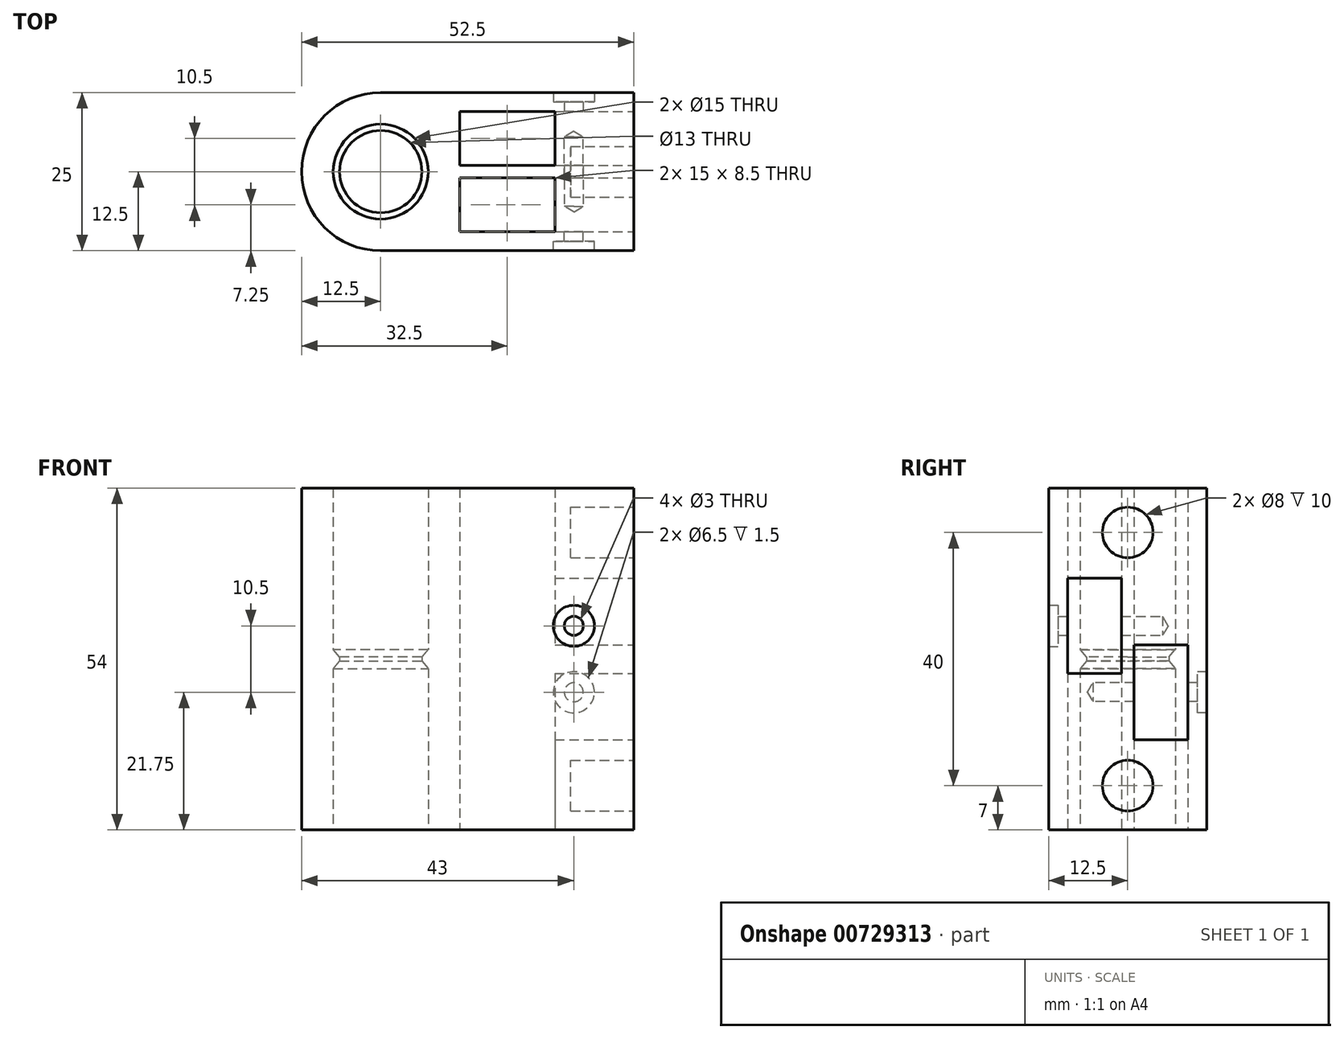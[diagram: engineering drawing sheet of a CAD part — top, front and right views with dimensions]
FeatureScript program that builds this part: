
annotation { "Feature Type Name" : "Feature", "Feature Type Description" : "" }
export const myFeature = defineFeature(function(context is Context, id is Id, definition is map)
    precondition{}
    {
        {
            var Q0;
            Q0=qCreatedBy(makeId("Top.planeOp"),FACE);
            var sketch = newSketch(context, id + "F0", { "sketchPlane" : qUnion([Q0])});
            skLineSegment(sketch, "E0.bottom", {"start": v(0, 0) * mm, "end": v(40, 0) * mm});
            skLineSegment(sketch, "E0.top", {"start": v(0, 25) * mm, "end": v(40, 25) * mm});
            skLineSegment(sketch, "E0.left", {"start": v(0, 0) * mm, "end": v(0, 25) * mm});
            skLineSegment(sketch, "E0.right", {"start": v(40, 0) * mm, "end": v(40, 25) * mm});
            skArc(sketch, "E1", {"start": v(0, 25) * mm, "mid": v(-12.5, 12.5) * mm, "end": v(0, 0) * mm});
            skCircle(sketch, "E2", {"center": v(0, 12.5) * mm, "radius": 7.5 * mm});
            skLineSegment(sketch, "E3.bottom", {"start": v(12.5, 22) * mm, "end": v(27.5, 22) * mm});
            skLineSegment(sketch, "E3.top", {"start": v(12.5, 3) * mm, "end": v(27.5, 3) * mm});
            skLineSegment(sketch, "E3.left", {"start": v(12.5, 22) * mm, "end": v(12.5, 3) * mm});
            skLineSegment(sketch, "E3.right", {"start": v(27.5, 22) * mm, "end": v(27.5, 3) * mm});
            skPoint(sketch, "E4", {"position": v(7.5, 12.5) * mm});
            skLineSegment(sketch, "E5.bottom", {"start": v(12.5, 13.5) * mm, "end": v(27.5, 13.5) * mm});
            skLineSegment(sketch, "E5.top", {"start": v(12.5, 11.5) * mm, "end": v(27.5, 11.5) * mm});
            skLineSegment(sketch, "E5.left", {"start": v(12.5, 13.5) * mm, "end": v(12.5, 11.5) * mm});
            skLineSegment(sketch, "E5.right", {"start": v(27.5, 13.5) * mm, "end": v(27.5, 11.5) * mm});
            skPoint(sketch, "E6", {"position": v(12.5, 12.5) * mm});
            skSolve(sketch);
        }
        {
            var Q0;
            {var subQ5=sQuery(id+"F0.wireOp",EDGE,"E0.bottom");Q0=makeQuery(id+"F0.imprint","IMPRINT",FACE,{"disambiguationData":[TD([[makeQuery(id+"F0.imprint","IMPRINT",EDGE,{"derivedFrom":subQ5}),1.0]])]});}
            var Q1;
            {var subQ0=sQuery(id+"F0.wireOp",EDGE,"E1");Q1=makeQuery(id+"F0.imprint","IMPRINT",FACE,{"disambiguationData":[TD([[makeQuery(id+"F0.imprint","IMPRINT",EDGE,{"derivedFrom":subQ0}),1.0]])]});}
            var Q2;
            {var subQ2=sQuery(id+"F0.wireOp",EDGE,"E5.bottom");Q2=makeQuery(id+"F0.imprint","IMPRINT",FACE,{"disambiguationData":[TD([[makeQuery(id+"F0.imprint","IMPRINT",EDGE,{"derivedFrom":subQ2}),-1.0]])]});}
            extrude(context, id + "F1", {"entities" : qUnion([Q0, Q1, Q2]), "depth" : 54 * mm, "offsetDistance" : 25 * mm});
        }
        {
            var Q0;
            Q0=makeQuery(id+"F1.opExtrude","SWEPT_FACE",FACE,{"disambiguationData":[OSD([sQuery(id+"F0.wireOp",EDGE,"E0.right")])]});
            var sketch = newSketch(context, id + "F2", { "sketchPlane" : qUnion([Q0])});
            skLineSegment(sketch, "E7.bottom", {"start": v(3, 39.75) * mm, "end": v(11.5, 39.75) * mm});
            skLineSegment(sketch, "E7.top", {"start": v(3, 24.75) * mm, "end": v(11.5, 24.75) * mm});
            skLineSegment(sketch, "E7.left", {"start": v(3, 39.75) * mm, "end": v(3, 24.75) * mm});
            skLineSegment(sketch, "E7.right", {"start": v(11.5, 39.75) * mm, "end": v(11.5, 24.75) * mm});
            skLineSegment(sketch, "E8.bottom", {"start": v(13.5, 29.25) * mm, "end": v(22, 29.25) * mm});
            skLineSegment(sketch, "E8.top", {"start": v(13.5, 14.25) * mm, "end": v(22, 14.25) * mm});
            skLineSegment(sketch, "E8.left", {"start": v(13.5, 29.25) * mm, "end": v(13.5, 14.25) * mm});
            skLineSegment(sketch, "E8.right", {"start": v(22, 29.25) * mm, "end": v(22, 14.25) * mm});
            skPoint(sketch, "E9", {"position": v(13.5, 27) * mm});
            skPoint(sketch, "E10", {"position": v(25, 27) * mm});
            skSolve(sketch);
        }
        {
            var Q0;
            Q0=makeQuery(id+"F2.imprint","IMPRINT",FACE,{"disambiguationData":[TD([[makeQuery(id+"F2.imprint","IMPRINT",EDGE,{"derivedFrom":sQuery(id+"F2.wireOp",EDGE,"E7.bottom")}),-1.0]])]});
            var Q1;
            Q1=makeQuery(id+"F2.imprint","IMPRINT",FACE,{"disambiguationData":[TD([[makeQuery(id+"F2.imprint","IMPRINT",EDGE,{"derivedFrom":sQuery(id+"F2.wireOp",EDGE,"E8.bottom")}),-1.0]])]});
            extrude(context, id + "F3", {"entities" : qUnion([Q0, Q1]), "operationType" : NewBodyOperationType.REMOVE, "endBound" : BoundingType.UP_TO_NEXT, "oppositeDirection" : true, "depth" : 25 * mm, "offsetDistance" : 25 * mm});
        }
        {
            var Q0;
            Q0=makeQuery(id+"F1.opExtrude","SWEPT_FACE",FACE,{"disambiguationData":[OSD([sQuery(id+"F0.wireOp",EDGE,"E0.bottom")])]});
            var sketch = newSketch(context, id + "F4", { "sketchPlane" : qUnion([Q0])});
            skPoint(sketch, "E11", {"position": v(30.5, 32.25) * mm});
            skSolve(sketch);
        }
        {
            var Q0;
            Q0=sQuery(id+"F4.wireOp",VERTEX,"E11");
            var Q1;
            Q1=makeQuery(id+"F1.opExtrude","SWEPT_BODY",BODY,{"disambiguationData":[OSD([sQuery(id+"F0.wireOp",EDGE,"E0.bottom"),sQuery(id+"F0.wireOp",EDGE,"E0.top"),sQuery(id+"F0.wireOp",EDGE,"E0.right"),sQuery(id+"F0.wireOp",EDGE,"E1"),sQuery(id+"F0.wireOp",EDGE,"E2"),sQuery(id+"F0.wireOp",EDGE,"E3.bottom"),sQuery(id+"F0.wireOp",EDGE,"E3.top"),sQuery(id+"F0.wireOp",EDGE,"E3.left"),sQuery(id+"F0.wireOp",EDGE,"E3.right")])]});
            hole(context, id + "F5", {"style" : HoleStyle.C_BORE, "endStyle" : HoleEndStyle.BLIND, "holeDiameter" : 3 * mm, "cBoreDiameter" : 6.5 * mm, "cBoreDepth" : 1.5 * mm, "majorDiameter" : 5 * mm, "holeDepth" : 18 * mm, "isTappedThrough" : true, "tappedDepth" : 12 * mm, "tapClearance" : 3, "locations" : qUnion([Q0]), "scope" : qUnion([Q1])});
        }
        {
            var Q0;
            Q0=makeQuery(id+"F1.opExtrude","SWEPT_FACE",FACE,{"disambiguationData":[OSD([sQuery(id+"F0.wireOp",EDGE,"E0.top")])]});
            var sketch = newSketch(context, id + "F6", { "sketchPlane" : qUnion([Q0])});
            skPoint(sketch, "E12", {"position": v(-30.5, 21.75) * mm});
            skSolve(sketch);
        }
        {
            var Q0;
            Q0=sQuery(id+"F6.wireOp",VERTEX,"E12");
            var Q1;
            Q1=makeQuery(id+"F1.opExtrude","SWEPT_BODY",BODY,{"disambiguationData":[OSD([sQuery(id+"F0.wireOp",EDGE,"E0.bottom"),sQuery(id+"F0.wireOp",EDGE,"E0.top"),sQuery(id+"F0.wireOp",EDGE,"E0.right"),sQuery(id+"F0.wireOp",EDGE,"E1"),sQuery(id+"F0.wireOp",EDGE,"E2"),sQuery(id+"F0.wireOp",EDGE,"E3.bottom"),sQuery(id+"F0.wireOp",EDGE,"E3.top"),sQuery(id+"F0.wireOp",EDGE,"E3.left"),sQuery(id+"F0.wireOp",EDGE,"E3.right")])]});
            hole(context, id + "F7", {"style" : HoleStyle.C_BORE, "endStyle" : HoleEndStyle.BLIND, "holeDiameter" : 3 * mm, "cBoreDiameter" : 6.5 * mm, "cBoreDepth" : 1.5 * mm, "majorDiameter" : 5 * mm, "holeDepth" : 18 * mm, "isTappedThrough" : true, "tappedDepth" : 12 * mm, "tapClearance" : 3, "locations" : qUnion([Q0]), "scope" : qUnion([Q1])});
        }
        {
            var Q0;
            Q0=makeQuery(id+"F1.opExtrude","SWEPT_FACE",FACE,{"disambiguationData":[OSD([sQuery(id+"F0.wireOp",EDGE,"E0.right")])]});
            var sketch = newSketch(context, id + "F8", { "sketchPlane" : qUnion([Q0])});
            skCircle(sketch, "E13", {"center": v(12.5, 47) * mm, "radius": 4 * mm});
            skCircle(sketch, "E14", {"center": v(12.5, 7) * mm, "radius": 4 * mm});
            skSolve(sketch);
        }
        {
            var Q0;
            Q0=makeQuery(id+"F8.imprint","IMPRINT",FACE,{"disambiguationData":[TD([[makeQuery(id+"F8.imprint","IMPRINT",EDGE,{"derivedFrom":sQuery(id+"F8.wireOp",EDGE,"E13")}),1.0]])]});
            var Q1;
            Q1=makeQuery(id+"F8.imprint","IMPRINT",FACE,{"disambiguationData":[TD([[makeQuery(id+"F8.imprint","IMPRINT",EDGE,{"derivedFrom":sQuery(id+"F8.wireOp",EDGE,"E14")}),1.0]])]});
            extrude(context, id + "F9", {"entities" : qUnion([Q0, Q1]), "operationType" : NewBodyOperationType.REMOVE, "oppositeDirection" : true, "depth" : 10 * mm, "offsetDistance" : 25 * mm});
        }
        {
            var Q0;
            Q0=qCreatedBy(makeId("Front.planeOp"),FACE);
            cPlane(context, id + "F10", {"entities" : qUnion([Q0]), "cplaneType" : CPlaneType.OFFSET, "offset" : 12.5 * mm, "oppositeDirection" : true, "width" : 150 * mm, "height" : 150 * mm});
        }
        {
            var Q0;
            Q0=qCreatedBy(id+"F10.planeOp",FACE);
            var sketch = newSketch(context, id + "F11", { "sketchPlane" : qUnion([Q0])});
            skLineSegment(sketch, "E15", {"start": v(7.5, 25.5) * mm, "end": v(7.5, 28.5) * mm});
            skLineSegment(sketch, "E16", {"start": v(0, 0) * mm, "end": v(0, 54) * mm, "construction": true});
            skPoint(sketch, "E17", {"position": v(0, 27) * mm});
            skPoint(sketch, "E18", {"position": v(7.5, 27) * mm});
            skLineSegment(sketch, "E19", {"start": v(7.5, 28.5) * mm, "end": v(6.5, 27.3) * mm});
            skLineSegment(sketch, "E20", {"start": v(6.5, 27.3) * mm, "end": v(6.5, 26.7) * mm});
            skLineSegment(sketch, "E21", {"start": v(6.5, 26.7) * mm, "end": v(7.5, 25.5) * mm});
            skPoint(sketch, "E22", {"position": v(6.5, 27) * mm});
            skSolve(sketch);
        }
        {
            var Q0;
            Q0=makeQuery(id+"F11.imprint","IMPRINT",FACE,{"disambiguationData":[TD([[makeQuery(id+"F11.imprint","IMPRINT",EDGE,{"derivedFrom":sQuery(id+"F11.wireOp",EDGE,"E15")}),1.0]])]});
            var Q1;
            Q1=sQuery(id+"F11.wireOp",EDGE,"E16");
            revolve(context, id + "F12", {"operationType" : NewBodyOperationType.ADD, "surfaceOperationType" : NewSurfaceOperationType.NEW, "entities" : qUnion([Q0]), "axis" : qUnion([Q1]), "revolveType" : RevolveType.FULL});
        }
    });
